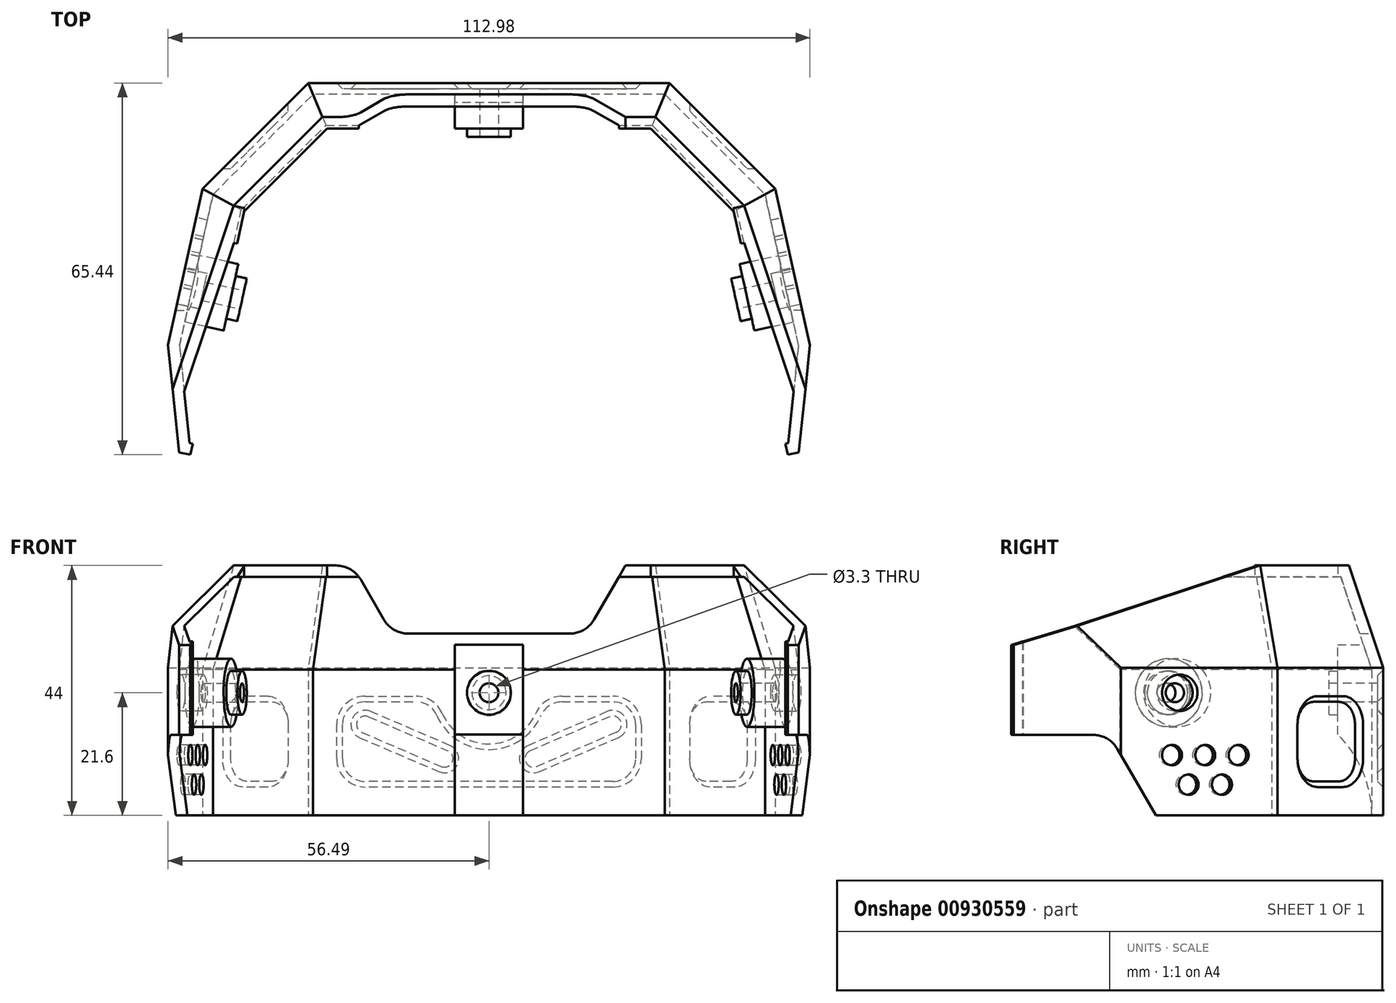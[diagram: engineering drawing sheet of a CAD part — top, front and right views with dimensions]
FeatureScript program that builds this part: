
annotation { "Feature Type Name" : "Feature", "Feature Type Description" : "" }
export const myFeature = defineFeature(function(context is Context, id is Id, definition is map)
    precondition{}
    {
        {
            var Q0;
            Q0=qCreatedBy(makeId("Top.planeOp"),FACE);
            var sketch = newSketch(context, id + "F0", { "sketchPlane" : qUnion([Q0])});
            skLineSegment(sketch, "E0", {"start": v(-18.54, 60) * mm, "end": v(18.54, 60) * mm, "construction": true});
            skArc(sketch, "E1", {"start": v(-18.54, 60) * mm, "mid": v(-31.06, 55.6) * mm, "end": v(-38.06, 44.32) * mm, "construction": true});
            skArc(sketch, "E2", {"start": v(38.06, 44.32) * mm, "mid": v(31.06, 55.6) * mm, "end": v(18.54, 60) * mm, "construction": true});
            skLineSegment(sketch, "E3", {"start": v(-38.06, 44.32) * mm, "end": v(-47.87, 0) * mm, "construction": true});
            skLineSegment(sketch, "E4", {"start": v(38.06, 44.32) * mm, "end": v(47.87, 0) * mm, "construction": true});
            skLineSegment(sketch, "E5", {"start": v(-44.1, 40.23) * mm, "end": v(-52.99, 0) * mm, "construction": true});
            skLineSegment(sketch, "E6", {"start": v(44.1, 40.23) * mm, "end": v(52.99, 0) * mm, "construction": true});
            skLineSegment(sketch, "E7", {"start": v(-44.1, 40.23) * mm, "end": v(-38.13, 44.03) * mm, "construction": true});
            skLineSegment(sketch, "E8", {"start": v(44.1, 40.23) * mm, "end": v(38.13, 44.03) * mm, "construction": true});
            skLineSegment(sketch, "E9", {"start": v(-52.99, 0) * mm, "end": v(52.99, 0) * mm, "construction": true});
            skLineSegment(sketch, "E10", {"start": v(-6, 60) * mm, "end": v(-6, 64) * mm, "construction": true});
            skLineSegment(sketch, "E11", {"start": v(-6, 64) * mm, "end": v(6, 64) * mm, "construction": true});
            skLineSegment(sketch, "E12", {"start": v(6, 64) * mm, "end": v(6, 60) * mm, "construction": true});
            skLineSegment(sketch, "E13", {"start": v(-45.4, 34.27) * mm, "end": v(-40.53, 33.19) * mm, "construction": true});
            skLineSegment(sketch, "E14", {"start": v(40.53, 33.19) * mm, "end": v(45.4, 34.27) * mm, "construction": true});
            skLineSegment(sketch, "E15", {"start": v(-28.48, 64) * mm, "end": v(28.48, 64) * mm});
            skLineSegment(sketch, "E16", {"start": v(-43.09, 49.39) * mm, "end": v(-52.56, 6.56) * mm});
            skLineSegment(sketch, "E17", {"start": v(43.09, 49.39) * mm, "end": v(52.56, 6.56) * mm});
            skLineSegment(sketch, "E18", {"start": v(-52.56, 6.56) * mm, "end": v(-60.37, 8.29) * mm});
            skLineSegment(sketch, "E19", {"start": v(-60.37, 8.29) * mm, "end": v(-50.4, 53.4) * mm});
            skLineSegment(sketch, "E20", {"start": v(52.56, 6.56) * mm, "end": v(60.37, 8.29) * mm});
            skLineSegment(sketch, "E21", {"start": v(60.37, 8.29) * mm, "end": v(50.4, 53.4) * mm});
            skLineSegment(sketch, "E22", {"start": v(-31.8, 72) * mm, "end": v(31.8, 72) * mm});
            skLineSegment(sketch, "E23", {"start": v(-28.48, 64) * mm, "end": v(-43.09, 49.39) * mm});
            skLineSegment(sketch, "E24", {"start": v(-50.4, 53.4) * mm, "end": v(-31.8, 72) * mm});
            skLineSegment(sketch, "E25", {"start": v(31.8, 72) * mm, "end": v(50.4, 53.4) * mm});
            skLineSegment(sketch, "E26", {"start": v(43.09, 49.39) * mm, "end": v(28.48, 64) * mm});
            skLineSegment(sketch, "E27", {"start": v(-45.4, 34.27) * mm, "end": v(-54.2, 36.21) * mm, "construction": true});
            skLineSegment(sketch, "E28", {"start": v(45.4, 34.27) * mm, "end": v(54.2, 36.21) * mm, "construction": true});
            skSolve(sketch);
        }
        {
            var Q0;
            Q0=qSketchRegion(id+"F0",true);
            extrude(context, id + "F1", {"entities" : qUnion([Q0]), "depth" : 44 * mm, "offsetDistance" : 25 * mm});
        }
        {
            var Q0;
            Q0=makeQuery(id+"F1.opExtrude","CAP_EDGE",EDGE,{"disambiguationData":[OSD([sQuery(id+"F0.wireOp",EDGE,"E19")])],"isStart":false});
            var Q1;
            Q1=makeQuery(id+"F1.opExtrude","CAP_EDGE",EDGE,{"disambiguationData":[OSD([sQuery(id+"F0.wireOp",EDGE,"E24")])],"isStart":false});
            var Q2;
            Q2=makeQuery(id+"F1.opExtrude","CAP_EDGE",EDGE,{"disambiguationData":[OSD([sQuery(id+"F0.wireOp",EDGE,"E22")])],"isStart":false});
            var Q3;
            Q3=makeQuery(id+"F1.opExtrude","CAP_EDGE",EDGE,{"disambiguationData":[OSD([sQuery(id+"F0.wireOp",EDGE,"E25")])],"isStart":false});
            var Q4;
            Q4=makeQuery(id+"F1.opExtrude","CAP_EDGE",EDGE,{"disambiguationData":[OSD([sQuery(id+"F0.wireOp",EDGE,"E21")])],"isStart":false});
            chamfer(context, id + "F2", {"entities" : qUnion([Q0, Q1, Q2, Q3, Q4]), "chamferType" : ChamferType.TWO_OFFSETS, "width1" : 18 * mm, "oppositeDirection" : false, "width2" : 6 * mm, "tangentPropagation" : true});
        }
        {
            var Q0;
            Q0=makeQuery(id+"F1.opExtrude","SWEPT_EDGE",EDGE,{"disambiguationData":[OSD([sQuery(id+"F0.wireOp",EDGE,"E18"),sQuery(id+"F0.wireOp",EDGE,"E19")])]});
            chamfer(context, id + "F3", {"entities" : qUnion([Q0]), "chamferType" : ChamferType.TWO_OFFSETS, "width1" : 6 * mm, "oppositeDirection" : false, "width2" : 18 * mm, "tangentPropagation" : true});
        }
        {
            var Q0;
            Q0=makeQuery(id+"F1.opExtrude","SWEPT_EDGE",EDGE,{"disambiguationData":[OSD([sQuery(id+"F0.wireOp",EDGE,"E20"),sQuery(id+"F0.wireOp",EDGE,"E21")])]});
            chamfer(context, id + "F4", {"entities" : qUnion([Q0]), "chamferType" : ChamferType.TWO_OFFSETS, "width1" : 18 * mm, "oppositeDirection" : false, "width2" : 6 * mm, "tangentPropagation" : true});
        }
        {
            var Q0;
            Q0=makeQuery(id+"F1.opExtrude","SWEPT_FACE",FACE,{"disambiguationData":[OSD([sQuery(id+"F0.wireOp",EDGE,"E15")])]});
            var Q1;
            Q1=makeQuery(id+"F1.opExtrude","SWEPT_FACE",FACE,{"disambiguationData":[OSD([sQuery(id+"F0.wireOp",EDGE,"E23")])]});
            var Q2;
            Q2=makeQuery(id+"F1.opExtrude","SWEPT_FACE",FACE,{"disambiguationData":[OSD([sQuery(id+"F0.wireOp",EDGE,"E16")])]});
            var Q3;
            Q3=makeQuery(id+"F1.opExtrude","SWEPT_FACE",FACE,{"disambiguationData":[OSD([sQuery(id+"F0.wireOp",EDGE,"E26")])]});
            var Q4;
            Q4=makeQuery(id+"F1.opExtrude","SWEPT_FACE",FACE,{"disambiguationData":[OSD([sQuery(id+"F0.wireOp",EDGE,"E17")])]});
            var Q5;
            Q5=makeQuery(id+"F1.opExtrude","CAP_FACE",FACE,{"disambiguationData":[OSD([sQuery(id+"F0.wireOp",EDGE,"E15"),sQuery(id+"F0.wireOp",EDGE,"E16"),sQuery(id+"F0.wireOp",EDGE,"E17"),sQuery(id+"F0.wireOp",EDGE,"E18"),sQuery(id+"F0.wireOp",EDGE,"E19"),sQuery(id+"F0.wireOp",EDGE,"E20"),sQuery(id+"F0.wireOp",EDGE,"E21"),sQuery(id+"F0.wireOp",EDGE,"E22"),sQuery(id+"F0.wireOp",EDGE,"E23"),sQuery(id+"F0.wireOp",EDGE,"E24"),sQuery(id+"F0.wireOp",EDGE,"E25"),sQuery(id+"F0.wireOp",EDGE,"E26")])],"isStart":true});
            shell(context, id + "F5", {"entities" : qUnion([Q0, Q1, Q2, Q3, Q4, Q5]), "thickness" : 2 * mm});
        }
        {
            var Q0;
            Q0=qCreatedBy(makeId("Right.planeOp"),FACE);
            var sketch = newSketch(context, id + "F6", { "sketchPlane" : qUnion([Q0])});
            skLineSegment(sketch, "E29", {"start": v(70, 25.68) * mm, "end": v(70, 0) * mm});
            skLineSegment(sketch, "E30", {"start": v(64, 14.24) * mm, "end": v(64, 30.04) * mm});
            skLineSegment(sketch, "E31", {"start": v(64, 30.04) * mm, "end": v(68.54, 30.04) * mm});
            skLineSegment(sketch, "E32", {"start": v(68.54, 30.04) * mm, "end": v(70, 25.68) * mm});
            skLineSegment(sketch, "E33.bottom", {"start": v(62, 30.04) * mm, "end": v(56, 30.04) * mm, "construction": true});
            skLineSegment(sketch, "E33.top", {"start": v(64, 14.24) * mm, "end": v(56, 14.24) * mm, "construction": true});
            skLineSegment(sketch, "E33.left", {"start": v(64, 28.04) * mm, "end": v(64, 14.24) * mm, "construction": true});
            skLineSegment(sketch, "E33.right", {"start": v(56, 30.04) * mm, "end": v(56, 14.24) * mm, "construction": true});
            skLineSegment(sketch, "E34", {"start": v(64, 28.04) * mm, "end": v(62, 30.04) * mm, "construction": true});
            skArc(sketch, "E35", {"start": v(70, 0) * mm, "mid": v(68.44, 7.73) * mm, "end": v(64, 14.24) * mm});
            skSolve(sketch);
        }
        {
            var Q0;
            Q0=qSketchRegion(id+"F6",true);
            extrude(context, id + "F7", {"entities" : qUnion([Q0]), "operationType" : NewBodyOperationType.ADD, "depth" : 6 * mm, "offsetDistance" : 25 * mm});
        }
        {
            var Q0;
            Q0=qSketchRegion(id+"F6",true);
            extrude(context, id + "F8", {"entities" : qUnion([Q0]), "operationType" : NewBodyOperationType.ADD, "oppositeDirection" : true, "depth" : 6 * mm, "offsetDistance" : 25 * mm});
        }
        {
            var Q0;
            {var subQ0=sQuery(id+"F6.wireOp",EDGE,"E30");Q0=makeQuery(id+"F8.boolean.opBoolean","MERGE",FACE,{"derivedFrom":[makeQuery(id+"F7.opExtrude","SWEPT_FACE",FACE,{"disambiguationData":[OSD([subQ0])]}),makeQuery(id+"F8.opExtrude","SWEPT_FACE",FACE,{"disambiguationData":[OSD([subQ0])]})]});}
            var sketch = newSketch(context, id + "F9", { "sketchPlane" : qUnion([Q0])});
            skCircle(sketch, "E36", {"center": v(0, 21.6) * mm, "radius": 3.85 * mm});
            skSolve(sketch);
        }
        {
            var Q0;
            Q0=qSketchRegion(id+"F9",true);
            extrude(context, id + "F10", {"entities" : qUnion([Q0]), "operationType" : NewBodyOperationType.ADD, "depth" : 1.5 * mm, "offsetDistance" : 25 * mm});
        }
        {
            var Q0;
            Q0=makeQuery(id+"F10.opExtrude","CAP_FACE",FACE,{"disambiguationData":[OSD([sQuery(id+"F9.wireOp",EDGE,"E36")])],"isStart":false});
            var sketch = newSketch(context, id + "F11", { "sketchPlane" : qUnion([Q0])});
            skCircle(sketch, "E37", {"center": v(0, 21.6) * mm, "radius": 1.65 * mm});
            skSolve(sketch);
        }
        {
            var Q0;
            Q0=qSketchRegion(id+"F11",true);
            extrude(context, id + "F12", {"entities" : qUnion([Q0]), "operationType" : NewBodyOperationType.REMOVE, "endBound" : BoundingType.UP_TO_NEXT, "oppositeDirection" : true, "depth" : 25 * mm, "offsetDistance" : 25 * mm});
        }
        {
            var Q0;
            Q0=makeQuery(id+"F1.opExtrude","SWEPT_FACE",FACE,{"disambiguationData":[OSD([sQuery(id+"F0.wireOp",EDGE,"E21")])]});
            var sketch = newSketch(context, id + "F13", { "sketchPlane" : qUnion([Q0])});
            skLineSegment(sketch, "E38", {"start": v(-4.95, 30) * mm, "end": v(39.5, 44) * mm});
            skLineSegment(sketch, "E39", {"start": v(39.5, 44) * mm, "end": v(-4.95, 44) * mm});
            skLineSegment(sketch, "E40", {"start": v(-4.95, 44) * mm, "end": v(-4.95, 30) * mm});
            skSolve(sketch);
        }
        {
            var Q0;
            Q0=qSketchRegion(id+"F13",true);
            var Q1;
            Q1=makeQuery(id+"F1.opExtrude","SWEPT_FACE",FACE,{"disambiguationData":[OSD([sQuery(id+"F0.wireOp",EDGE,"E17")])]});
            extrude(context, id + "F14", {"entities" : qUnion([Q0]), "operationType" : NewBodyOperationType.REMOVE, "endBound" : BoundingType.UP_TO_SURFACE, "oppositeDirection" : true, "depth" : 25 * mm, "endBoundEntityFace" : qUnion([Q1]), "offsetDistance" : 25 * mm});
        }
        {
            var Q0;
            Q0=makeQuery(id+"F1.opExtrude","SWEPT_FACE",FACE,{"disambiguationData":[OSD([sQuery(id+"F0.wireOp",EDGE,"E19")])]});
            var sketch = newSketch(context, id + "F15", { "sketchPlane" : qUnion([Q0])});
            skLineSegment(sketch, "E41", {"start": v(-39.5, 44) * mm, "end": v(4.95, 44) * mm});
            skLineSegment(sketch, "E42", {"start": v(4.95, 44) * mm, "end": v(4.95, 30) * mm});
            skLineSegment(sketch, "E43", {"start": v(4.95, 30) * mm, "end": v(-39.5, 44) * mm});
            skSolve(sketch);
        }
        {
            var Q0;
            Q0=qSketchRegion(id+"F15",true);
            var Q1;
            Q1=makeQuery(id+"F1.opExtrude","SWEPT_FACE",FACE,{"disambiguationData":[OSD([sQuery(id+"F0.wireOp",EDGE,"E16")])]});
            extrude(context, id + "F16", {"entities" : qUnion([Q0]), "operationType" : NewBodyOperationType.REMOVE, "endBound" : BoundingType.UP_TO_SURFACE, "oppositeDirection" : true, "depth" : 25 * mm, "endBoundEntityFace" : qUnion([Q1]), "offsetDistance" : 25 * mm});
        }
        {
            var Q0;
            Q0=qCreatedBy(makeId("Right.planeOp"),FACE);
            var sketch = newSketch(context, id + "F17", { "sketchPlane" : qUnion([Q0])});
            skLineSegment(sketch, "E44", {"start": v(32, 0) * mm, "end": v(23.8, 14.2) * mm});
            skLineSegment(sketch, "E45", {"start": v(23.8, 14.2) * mm, "end": v(6.56, 14.2) * mm});
            skLineSegment(sketch, "E46", {"start": v(6.56, 14.2) * mm, "end": v(6.56, 0) * mm});
            skLineSegment(sketch, "E47", {"start": v(6.56, 0) * mm, "end": v(32, 0) * mm});
            skCircle(sketch, "E48", {"center": v(14.7, 7) * mm, "radius": 10 * mm, "construction": true});
            skSolve(sketch);
        }
        {
            var Q0;
            Q0=qSketchRegion(id+"F17",true);
            var Q1;
            Q1=makeQuery(id+"F3.opChamfer","BLEND_FACE",FACE,{"disambiguationData":[OSD([sQuery(id+"F0.wireOp",EDGE,"E18"),sQuery(id+"F0.wireOp",EDGE,"E19")])]});
            extrude(context, id + "F18", {"entities" : qUnion([Q0]), "operationType" : NewBodyOperationType.REMOVE, "endBound" : BoundingType.UP_TO_SURFACE, "oppositeDirection" : true, "depth" : 25 * mm, "endBoundEntityFace" : qUnion([Q1]), "offsetDistance" : 25 * mm});
        }
        {
            var Q0;
            Q0=qSketchRegion(id+"F17",true);
            var Q1;
            Q1=makeQuery(id+"F4.opChamfer","BLEND_FACE",FACE,{"disambiguationData":[OSD([sQuery(id+"F0.wireOp",EDGE,"E20"),sQuery(id+"F0.wireOp",EDGE,"E21")])]});
            extrude(context, id + "F19", {"entities" : qUnion([Q0]), "operationType" : NewBodyOperationType.REMOVE, "endBound" : BoundingType.UP_TO_SURFACE, "depth" : 25 * mm, "endBoundEntityFace" : qUnion([Q1]), "offsetDistance" : 25 * mm});
        }
        {
            var Q0;
            Q0=makeQuery(id+"F1.opExtrude","SWEPT_FACE",FACE,{"disambiguationData":[OSD([sQuery(id+"F0.wireOp",EDGE,"E22")])]});
            var sketch = newSketch(context, id + "F20", { "sketchPlane" : qUnion([Q0])});
            skLineSegment(sketch, "E49", {"start": v(-24, 44) * mm, "end": v(24, 44) * mm});
            skLineSegment(sketch, "E50", {"start": v(24, 44) * mm, "end": v(17.07, 32) * mm});
            skLineSegment(sketch, "E51", {"start": v(17.07, 32) * mm, "end": v(-17.07, 32) * mm});
            skLineSegment(sketch, "E52", {"start": v(-17.07, 32) * mm, "end": v(-24, 44) * mm});
            skSolve(sketch);
        }
        {
            var Q0;
            Q0=qSketchRegion(id+"F20",true);
            var Q1;
            Q1=makeQuery(id+"F1.opExtrude","SWEPT_FACE",FACE,{"disambiguationData":[OSD([sQuery(id+"F0.wireOp",EDGE,"E15")])]});
            extrude(context, id + "F21", {"entities" : qUnion([Q0]), "operationType" : NewBodyOperationType.REMOVE, "endBound" : BoundingType.UP_TO_SURFACE, "oppositeDirection" : true, "depth" : 25 * mm, "endBoundEntityFace" : qUnion([Q1]), "offsetDistance" : 25 * mm});
        }
        {
            var Q0;
            Q0=makeQuery(id+"F21.boolean.opBoolean","COPY",EDGE,{"derivedFrom":makeQuery(id+"F21.opExtrude","SWEPT_EDGE",EDGE,{"disambiguationData":[OSD([sQuery(id+"F20.wireOp",EDGE,"E51"),sQuery(id+"F20.wireOp",EDGE,"E52")])]})});
            var Q1;
            Q1=makeQuery(id+"F21.boolean.opBoolean","COPY",EDGE,{"derivedFrom":makeQuery(id+"F21.opExtrude","SWEPT_EDGE",EDGE,{"disambiguationData":[OSD([sQuery(id+"F20.wireOp",EDGE,"E50"),sQuery(id+"F20.wireOp",EDGE,"E51")])]})});
            var Q2;
            Q2=makeQuery(id+"F21.boolean.opBoolean","COPY",EDGE,{"derivedFrom":makeQuery(id+"F21.opExtrude","SWEPT_EDGE",EDGE,{"disambiguationData":[OSD([sQuery(id+"F20.wireOp",EDGE,"E49"),sQuery(id+"F20.wireOp",EDGE,"E52")])]})});
            var Q3;
            Q3=makeQuery(id+"F21.boolean.opBoolean","COPY",EDGE,{"derivedFrom":makeQuery(id+"F21.opExtrude","SWEPT_EDGE",EDGE,{"disambiguationData":[OSD([sQuery(id+"F20.wireOp",EDGE,"E49"),sQuery(id+"F20.wireOp",EDGE,"E50")])]})});
            fillet(context, id + "F22", {"entities" : qUnion([Q0, Q1, Q2, Q3]), "radius" : 5 * mm, "tangentPropagation" : true, "allowEdgeOverflow" : false});
        }
        {
            var Q0;
            Q0=makeQuery(id+"F1.opExtrude","SWEPT_FACE",FACE,{"disambiguationData":[OSD([sQuery(id+"F0.wireOp",EDGE,"E22")])]});
            var sketch = newSketch(context, id + "F23", { "sketchPlane" : qUnion([Q0])});
            skLineSegment(sketch, "E53", {"start": v(-26.8, 16) * mm, "end": v(-26.8, 10) * mm});
            skLineSegment(sketch, "E54", {"start": v(-21.8, 5) * mm, "end": v(21.8, 5) * mm});
            skLineSegment(sketch, "E55", {"start": v(26.8, 10) * mm, "end": v(26.8, 16) * mm});
            skLineSegment(sketch, "E56", {"start": v(21.8, 21) * mm, "end": v(12.83, 21) * mm});
            skLineSegment(sketch, "E57", {"start": v(-12.83, 21) * mm, "end": v(-21.8, 21) * mm});
            skCircle(sketch, "E58", {"center": v(0, 21.6) * mm, "radius": 4 * mm});
            skArc(sketch, "E59", {"start": v(-8.25, 18) * mm, "mid": v(0, 12.6) * mm, "end": v(8.25, 18) * mm});
            skLineSegment(sketch, "E60", {"start": v(-21.2, 17.38) * mm, "end": v(-7.25, 11.38) * mm});
            skLineSegment(sketch, "E61", {"start": v(-22.38, 14.62) * mm, "end": v(-8.43, 8.62) * mm});
            skArc(sketch, "E62", {"start": v(-21.2, 17.38) * mm, "mid": v(-23.17, 16.6) * mm, "end": v(-22.38, 14.62) * mm});
            skArc(sketch, "E63", {"start": v(-8.43, 8.62) * mm, "mid": v(-6.46, 9.4) * mm, "end": v(-7.25, 11.38) * mm});
            skPoint(sketch, "E64.visualSharp", {"position": v(-26.8, 21) * mm});
            skArc(sketch, "E64.filletArc", {"start": v(-21.8, 21) * mm, "mid": v(-25.33, 19.54) * mm, "end": v(-26.8, 16) * mm});
            skPoint(sketch, "E65.visualSharp", {"position": v(-26.8, 5) * mm});
            skArc(sketch, "E65.filletArc", {"start": v(-26.8, 10) * mm, "mid": v(-25.33, 6.46) * mm, "end": v(-21.8, 5) * mm});
            skPoint(sketch, "E66.visualSharp", {"position": v(-8.98, 21) * mm});
            skArc(sketch, "E66.filletArc", {"start": v(-8.25, 18) * mm, "mid": v(-10.1, 20.18) * mm, "end": v(-12.83, 21) * mm});
            skPoint(sketch, "E67.visualSharp", {"position": v(8.98, 21) * mm});
            skArc(sketch, "E67.filletArc", {"start": v(12.83, 21) * mm, "mid": v(10.1, 20.18) * mm, "end": v(8.25, 18) * mm});
            skPoint(sketch, "E68.visualSharp", {"position": v(26.8, 21) * mm});
            skArc(sketch, "E68.filletArc", {"start": v(26.8, 16) * mm, "mid": v(25.33, 19.54) * mm, "end": v(21.8, 21) * mm});
            skPoint(sketch, "E69.visualSharp", {"position": v(26.8, 5) * mm});
            skArc(sketch, "E69.filletArc", {"start": v(21.8, 5) * mm, "mid": v(25.33, 6.46) * mm, "end": v(26.8, 10) * mm});
            skLineSegment(sketch, "E70", {"start": v(21.2, 17.38) * mm, "end": v(7.25, 11.38) * mm});
            skLineSegment(sketch, "E71", {"start": v(22.38, 14.62) * mm, "end": v(8.43, 8.62) * mm});
            skArc(sketch, "E72", {"start": v(22.38, 14.62) * mm, "mid": v(23.17, 16.6) * mm, "end": v(21.2, 17.38) * mm});
            skArc(sketch, "E73", {"start": v(7.25, 11.38) * mm, "mid": v(6.46, 9.4) * mm, "end": v(8.43, 8.62) * mm});
            skLineSegment(sketch, "E74", {"start": v(-7.84, 10) * mm, "end": v(-7.84, 5) * mm, "construction": true});
            skLineSegment(sketch, "E75", {"start": v(-7.84, 10) * mm, "end": v(-5.04, 14.14) * mm, "construction": true});
            skLineSegment(sketch, "E76", {"start": v(7.84, 10) * mm, "end": v(5.04, 14.14) * mm, "construction": true});
            skLineSegment(sketch, "E77", {"start": v(7.84, 10) * mm, "end": v(7.84, 5) * mm, "construction": true});
            skSolve(sketch);
        }
        {
            var Q0;
            Q0=qSketchRegion(id+"F23",true);
            extrude(context, id + "F24", {"entities" : qUnion([Q0]), "operationType" : NewBodyOperationType.REMOVE, "oppositeDirection" : true, "depth" : 1 * mm, "offsetDistance" : 25 * mm});
        }
        {
            var Q0;
            Q0=makeQuery(id+"F24.boolean.opBoolean","COPY",EDGE,{"derivedFrom":makeQuery(id+"F24.opExtrude","CAP_EDGE",EDGE,{"disambiguationData":[OSD([sQuery(id+"F23.wireOp",EDGE,"E59")])],"isStart":false})});
            var Q1;
            Q1=makeQuery(id+"F24.boolean.opBoolean","COPY",EDGE,{"derivedFrom":makeQuery(id+"F24.opExtrude","CAP_EDGE",EDGE,{"disambiguationData":[OSD([sQuery(id+"F23.wireOp",EDGE,"E61")])],"isStart":false})});
            var Q2;
            Q2=makeQuery(id+"F24.boolean.opBoolean","COPY",EDGE,{"derivedFrom":makeQuery(id+"F24.opExtrude","CAP_EDGE",EDGE,{"disambiguationData":[OSD([sQuery(id+"F23.wireOp",EDGE,"E71")])],"isStart":false})});
            var Q3;
            Q3=makeQuery(id+"F24.boolean.opBoolean","COPY",EDGE,{"derivedFrom":makeQuery(id+"F24.opExtrude","CAP_EDGE",EDGE,{"disambiguationData":[OSD([sQuery(id+"F23.wireOp",EDGE,"E58")])],"isStart":false})});
            chamfer(context, id + "F25", {"entities" : qUnion([Q0, Q1, Q2, Q3]), "width" : 1 * mm, "tangentPropagation" : true});
        }
        {
            var Q0;
            Q0=makeQuery(id+"F1.opExtrude","SWEPT_FACE",FACE,{"disambiguationData":[OSD([sQuery(id+"F0.wireOp",EDGE,"E25")])]});
            var sketch = newSketch(context, id + "F26", { "sketchPlane" : qUnion([Q0])});
            skLineSegment(sketch, "E78.bottom", {"start": v(12.12, 21) * mm, "end": v(18.43, 21) * mm});
            skLineSegment(sketch, "E78.top", {"start": v(12.12, 5) * mm, "end": v(18.43, 5) * mm});
            skLineSegment(sketch, "E78.left", {"start": v(7.12, 16) * mm, "end": v(7.12, 10) * mm});
            skLineSegment(sketch, "E78.right", {"start": v(23.43, 16) * mm, "end": v(23.43, 10) * mm});
            skPoint(sketch, "E79.visualSharp", {"position": v(7.12, 21) * mm});
            skArc(sketch, "E79.filletArc", {"start": v(12.12, 21) * mm, "mid": v(8.59, 19.54) * mm, "end": v(7.12, 16) * mm});
            skPoint(sketch, "E80.visualSharp", {"position": v(7.12, 5) * mm});
            skArc(sketch, "E80.filletArc", {"start": v(7.12, 10) * mm, "mid": v(8.59, 6.46) * mm, "end": v(12.12, 5) * mm});
            skPoint(sketch, "E81.visualSharp", {"position": v(23.43, 5) * mm});
            skArc(sketch, "E81.filletArc", {"start": v(18.43, 5) * mm, "mid": v(21.97, 6.46) * mm, "end": v(23.43, 10) * mm});
            skPoint(sketch, "E82.visualSharp", {"position": v(23.43, 21) * mm});
            skArc(sketch, "E82.filletArc", {"start": v(23.43, 16) * mm, "mid": v(21.97, 19.54) * mm, "end": v(18.43, 21) * mm});
            skSolve(sketch);
        }
        {
            var Q0;
            Q0=qSketchRegion(id+"F26",true);
            extrude(context, id + "F27", {"entities" : qUnion([Q0]), "operationType" : NewBodyOperationType.REMOVE, "oppositeDirection" : true, "depth" : 1 * mm, "offsetDistance" : 25 * mm});
        }
        {
            var Q0;
            Q0=makeQuery(id+"F27.boolean.opBoolean","COPY",EDGE,{"derivedFrom":makeQuery(id+"F27.opExtrude","CAP_EDGE",EDGE,{"disambiguationData":[OSD([sQuery(id+"F26.wireOp",EDGE,"E79.filletArc")])],"isStart":false})});
            chamfer(context, id + "F28", {"entities" : qUnion([Q0]), "width" : 1 * mm, "tangentPropagation" : true});
        }
        {
            var Q0;
            Q0=makeQuery(id+"F1.opExtrude","SWEPT_FACE",FACE,{"disambiguationData":[OSD([sQuery(id+"F0.wireOp",EDGE,"E24")])]});
            var sketch = newSketch(context, id + "F29", { "sketchPlane" : qUnion([Q0])});
            skLineSegment(sketch, "E83.bottom", {"start": v(-18.43, 21) * mm, "end": v(-12.12, 21) * mm});
            skLineSegment(sketch, "E83.top", {"start": v(-18.43, 5) * mm, "end": v(-12.12, 5) * mm});
            skLineSegment(sketch, "E83.left", {"start": v(-23.43, 16) * mm, "end": v(-23.43, 10) * mm});
            skLineSegment(sketch, "E83.right", {"start": v(-7.12, 16) * mm, "end": v(-7.12, 10) * mm});
            skPoint(sketch, "E84.visualSharp", {"position": v(-23.43, 21) * mm});
            skArc(sketch, "E84.filletArc", {"start": v(-18.43, 21) * mm, "mid": v(-21.97, 19.54) * mm, "end": v(-23.43, 16) * mm});
            skPoint(sketch, "E85.visualSharp", {"position": v(-23.43, 5) * mm});
            skArc(sketch, "E85.filletArc", {"start": v(-23.43, 10) * mm, "mid": v(-21.97, 6.46) * mm, "end": v(-18.43, 5) * mm});
            skPoint(sketch, "E86.visualSharp", {"position": v(-7.12, 5) * mm});
            skArc(sketch, "E86.filletArc", {"start": v(-12.12, 5) * mm, "mid": v(-8.59, 6.46) * mm, "end": v(-7.12, 10) * mm});
            skPoint(sketch, "E87.visualSharp", {"position": v(-7.12, 21) * mm});
            skArc(sketch, "E87.filletArc", {"start": v(-7.12, 16) * mm, "mid": v(-8.59, 19.54) * mm, "end": v(-12.12, 21) * mm});
            skSolve(sketch);
        }
        {
            var Q0;
            Q0=qSketchRegion(id+"F29",true);
            extrude(context, id + "F30", {"entities" : qUnion([Q0]), "operationType" : NewBodyOperationType.REMOVE, "oppositeDirection" : true, "depth" : 1 * mm, "offsetDistance" : 25 * mm});
        }
        {
            var Q0;
            Q0=makeQuery(id+"F30.boolean.opBoolean","COPY",EDGE,{"derivedFrom":makeQuery(id+"F30.opExtrude","CAP_EDGE",EDGE,{"disambiguationData":[OSD([sQuery(id+"F29.wireOp",EDGE,"E84.filletArc")])],"isStart":false})});
            chamfer(context, id + "F31", {"entities" : qUnion([Q0]), "width" : 1 * mm, "tangentPropagation" : true});
        }
        {
            var Q0;
            {var subQ0=sQuery(id+"F0.wireOp",EDGE,"E19");Q0=makeQuery(id+"F5.opShell","OFFSET_FACE",FACE,{"disambiguationData":[OSD([subQ0]),TDD([makeQuery(id+"F1.opExtrude","SWEPT_FACE",FACE,{"disambiguationData":[OSD([subQ0])]})])]});}
            var sketch = newSketch(context, id + "F32", { "sketchPlane" : qUnion([Q0])});
            skCircle(sketch, "E88", {"center": v(23.65, 21.6) * mm, "radius": 6 * mm});
            skSolve(sketch);
        }
        {
            var Q0;
            Q0=qSketchRegion(id+"F32",true);
            extrude(context, id + "F33", {"entities" : qUnion([Q0]), "operationType" : NewBodyOperationType.ADD, "depth" : 7 * mm, "offsetDistance" : 25 * mm});
        }
        {
            var Q0;
            {var subQ0=sQuery(id+"F0.wireOp",EDGE,"E21");Q0=makeQuery(id+"F5.opShell","OFFSET_FACE",FACE,{"disambiguationData":[OSD([subQ0]),TDD([makeQuery(id+"F1.opExtrude","SWEPT_FACE",FACE,{"disambiguationData":[OSD([subQ0])]})])]});}
            var sketch = newSketch(context, id + "F34", { "sketchPlane" : qUnion([Q0])});
            skCircle(sketch, "E89", {"center": v(-23.65, 21.6) * mm, "radius": 6 * mm});
            skSolve(sketch);
        }
        {
            var Q0;
            Q0=qSketchRegion(id+"F34",true);
            extrude(context, id + "F35", {"entities" : qUnion([Q0]), "operationType" : NewBodyOperationType.ADD, "depth" : 7 * mm, "offsetDistance" : 25 * mm});
        }
        {
            var Q0;
            Q0=makeQuery(id+"F35.opExtrude","CAP_FACE",FACE,{"disambiguationData":[OSD([sQuery(id+"F34.wireOp",EDGE,"E89")])],"isStart":false});
            var sketch = newSketch(context, id + "F36", { "sketchPlane" : qUnion([Q0])});
            skCircle(sketch, "E90", {"center": v(-23.65, 21.6) * mm, "radius": 3.85 * mm});
            skSolve(sketch);
        }
        {
            var Q0;
            Q0=qSketchRegion(id+"F36",true);
            extrude(context, id + "F37", {"entities" : qUnion([Q0]), "operationType" : NewBodyOperationType.ADD, "depth" : 2 * mm, "offsetDistance" : 25 * mm});
        }
        {
            var Q0;
            Q0=makeQuery(id+"F33.opExtrude","CAP_FACE",FACE,{"disambiguationData":[OSD([sQuery(id+"F32.wireOp",EDGE,"E88")])],"isStart":false});
            var sketch = newSketch(context, id + "F38", { "sketchPlane" : qUnion([Q0])});
            skCircle(sketch, "E91", {"center": v(23.65, 21.6) * mm, "radius": 3.85 * mm});
            skSolve(sketch);
        }
        {
            var Q0;
            Q0=qSketchRegion(id+"F38",true);
            extrude(context, id + "F39", {"entities" : qUnion([Q0]), "operationType" : NewBodyOperationType.ADD, "depth" : 2 * mm, "offsetDistance" : 25 * mm});
        }
        {
            var Q0;
            Q0=makeQuery(id+"F37.opExtrude","CAP_FACE",FACE,{"disambiguationData":[OSD([sQuery(id+"F36.wireOp",EDGE,"E90")])],"isStart":false});
            var sketch = newSketch(context, id + "F40", { "sketchPlane" : qUnion([Q0])});
            skCircle(sketch, "E92", {"center": v(-23.65, 21.6) * mm, "radius": 1.65 * mm});
            skSolve(sketch);
        }
        {
            var Q0;
            Q0=qSketchRegion(id+"F40",true);
            extrude(context, id + "F41", {"entities" : qUnion([Q0]), "operationType" : NewBodyOperationType.REMOVE, "endBound" : BoundingType.UP_TO_NEXT, "oppositeDirection" : true, "depth" : 25 * mm, "offsetDistance" : 25 * mm});
        }
        {
            var Q0;
            Q0=makeQuery(id+"F39.opExtrude","CAP_FACE",FACE,{"disambiguationData":[OSD([sQuery(id+"F38.wireOp",EDGE,"E91")])],"isStart":false});
            var sketch = newSketch(context, id + "F42", { "sketchPlane" : qUnion([Q0])});
            skCircle(sketch, "E93", {"center": v(23.65, 21.6) * mm, "radius": 1.65 * mm});
            skSolve(sketch);
        }
        {
            var Q0;
            Q0=qSketchRegion(id+"F42",true);
            extrude(context, id + "F43", {"entities" : qUnion([Q0]), "operationType" : NewBodyOperationType.REMOVE, "endBound" : BoundingType.UP_TO_NEXT, "oppositeDirection" : true, "depth" : 25 * mm, "offsetDistance" : 25 * mm});
        }
        {
            var Q0;
            Q0=makeQuery(id+"F1.opExtrude","SWEPT_FACE",FACE,{"disambiguationData":[OSD([sQuery(id+"F0.wireOp",EDGE,"E19")])]});
            var sketch = newSketch(context, id + "F44", { "sketchPlane" : qUnion([Q0])});
            skCircle(sketch, "E94", {"center": v(-23.65, 21.6) * mm, "radius": 3.2 * mm});
            skSolve(sketch);
        }
        {
            var Q0;
            Q0=qSketchRegion(id+"F44",true);
            extrude(context, id + "F45", {"entities" : qUnion([Q0]), "operationType" : NewBodyOperationType.REMOVE, "oppositeDirection" : true, "depth" : 4 * mm, "offsetDistance" : 25 * mm});
        }
        {
            var Q0;
            Q0=makeQuery(id+"F1.opExtrude","SWEPT_FACE",FACE,{"disambiguationData":[OSD([sQuery(id+"F0.wireOp",EDGE,"E21")])]});
            var sketch = newSketch(context, id + "F46", { "sketchPlane" : qUnion([Q0])});
            skCircle(sketch, "E95", {"center": v(23.65, 21.6) * mm, "radius": 3.2 * mm});
            skSolve(sketch);
        }
        {
            var Q0;
            Q0=qSketchRegion(id+"F46",true);
            extrude(context, id + "F47", {"entities" : qUnion([Q0]), "operationType" : NewBodyOperationType.REMOVE, "oppositeDirection" : true, "depth" : 4 * mm, "offsetDistance" : 25 * mm});
        }
        {
            var Q0;
            Q0=makeQuery(id+"F1.opExtrude","SWEPT_FACE",FACE,{"disambiguationData":[OSD([sQuery(id+"F0.wireOp",EDGE,"E21")])]});
            var sketch = newSketch(context, id + "F48", { "sketchPlane" : qUnion([Q0])});
            skLineSegment(sketch, "E96", {"start": v(22.25, 10.63) * mm, "end": v(25.25, 5.43) * mm, "construction": true});
            skLineSegment(sketch, "E97", {"start": v(25.25, 5.43) * mm, "end": v(28.25, 10.63) * mm, "construction": true});
            skLineSegment(sketch, "E98", {"start": v(28.25, 10.63) * mm, "end": v(22.25, 10.63) * mm, "construction": true});
            skLineSegment(sketch, "E99", {"start": v(28.25, 10.63) * mm, "end": v(34.25, 10.63) * mm, "construction": true});
            skLineSegment(sketch, "E100", {"start": v(34.25, 10.63) * mm, "end": v(31.25, 5.43) * mm, "construction": true});
            skLineSegment(sketch, "E101", {"start": v(31.25, 5.43) * mm, "end": v(28.25, 10.63) * mm, "construction": true});
            skLineSegment(sketch, "E102", {"start": v(25.25, 5.43) * mm, "end": v(31.25, 5.43) * mm, "construction": true});
            skCircle(sketch, "E103", {"center": v(22.25, 10.63) * mm, "radius": 1.8 * mm});
            skCircle(sketch, "E104", {"center": v(28.25, 10.63) * mm, "radius": 1.8 * mm});
            skCircle(sketch, "E105", {"center": v(34.25, 10.63) * mm, "radius": 1.8 * mm});
            skCircle(sketch, "E106", {"center": v(25.25, 5.43) * mm, "radius": 1.8 * mm});
            skCircle(sketch, "E107", {"center": v(31.25, 5.43) * mm, "radius": 1.8 * mm});
            skLineSegment(sketch, "E108", {"start": v(22.25, 10.63) * mm, "end": v(13.05, 10.63) * mm, "construction": true});
            skLineSegment(sketch, "E109", {"start": v(34.25, 10.63) * mm, "end": v(41.25, 10.63) * mm, "construction": true});
            skSolve(sketch);
        }
        {
            var Q0;
            Q0=qSketchRegion(id+"F48",true);
            extrude(context, id + "F49", {"entities" : qUnion([Q0]), "operationType" : NewBodyOperationType.REMOVE, "endBound" : BoundingType.UP_TO_NEXT, "oppositeDirection" : true, "depth" : 25 * mm, "offsetDistance" : 25 * mm});
        }
        {
            var Q0;
            Q0=makeQuery(id+"F1.opExtrude","SWEPT_FACE",FACE,{"disambiguationData":[OSD([sQuery(id+"F0.wireOp",EDGE,"E19")])]});
            var sketch = newSketch(context, id + "F50", { "sketchPlane" : qUnion([Q0])});
            skLineSegment(sketch, "E110", {"start": v(-34.25, 10.63) * mm, "end": v(-28.25, 10.63) * mm, "construction": true});
            skLineSegment(sketch, "E111", {"start": v(-28.25, 10.63) * mm, "end": v(-22.25, 10.63) * mm, "construction": true});
            skLineSegment(sketch, "E112", {"start": v(-22.25, 10.63) * mm, "end": v(-25.25, 5.43) * mm, "construction": true});
            skLineSegment(sketch, "E113", {"start": v(-25.25, 5.43) * mm, "end": v(-28.25, 10.63) * mm, "construction": true});
            skLineSegment(sketch, "E114", {"start": v(-34.25, 10.63) * mm, "end": v(-31.25, 5.43) * mm, "construction": true});
            skLineSegment(sketch, "E115", {"start": v(-31.25, 5.43) * mm, "end": v(-28.25, 10.63) * mm, "construction": true});
            skLineSegment(sketch, "E116", {"start": v(-31.25, 5.43) * mm, "end": v(-25.25, 5.43) * mm, "construction": true});
            skLineSegment(sketch, "E117", {"start": v(-22.25, 10.63) * mm, "end": v(-13.05, 10.63) * mm, "construction": true});
            skCircle(sketch, "E118", {"center": v(-34.25, 10.63) * mm, "radius": 1.8 * mm});
            skCircle(sketch, "E119", {"center": v(-31.25, 5.43) * mm, "radius": 1.8 * mm});
            skCircle(sketch, "E120", {"center": v(-28.25, 10.63) * mm, "radius": 1.8 * mm});
            skCircle(sketch, "E121", {"center": v(-25.25, 5.43) * mm, "radius": 1.8 * mm});
            skCircle(sketch, "E122", {"center": v(-22.25, 10.63) * mm, "radius": 1.8 * mm});
            skLineSegment(sketch, "E123", {"start": v(-34.25, 10.63) * mm, "end": v(-41.25, 10.63) * mm, "construction": true});
            skSolve(sketch);
        }
        {
            var Q0;
            Q0=qSketchRegion(id+"F50",true);
            extrude(context, id + "F51", {"entities" : qUnion([Q0]), "operationType" : NewBodyOperationType.REMOVE, "endBound" : BoundingType.UP_TO_NEXT, "oppositeDirection" : true, "depth" : 25 * mm, "offsetDistance" : 25 * mm});
        }
        {
            var Q0;
            Q0=makeQuery(id+"F19.boolean.opBoolean","COPY",EDGE,{"derivedFrom":makeQuery(id+"F19.opExtrude","SWEPT_EDGE",EDGE,{"disambiguationData":[OSD([sQuery(id+"F17.wireOp",EDGE,"E44"),sQuery(id+"F17.wireOp",EDGE,"E45")])]})});
            var Q1;
            Q1=makeQuery(id+"F18.boolean.opBoolean","COPY",EDGE,{"derivedFrom":makeQuery(id+"F18.opExtrude","SWEPT_EDGE",EDGE,{"disambiguationData":[OSD([sQuery(id+"F17.wireOp",EDGE,"E44"),sQuery(id+"F17.wireOp",EDGE,"E45")])]})});
            fillet(context, id + "F52", {"entities" : qUnion([Q0, Q1]), "radius" : 5 * mm, "tangentPropagation" : true, "allowEdgeOverflow" : false});
        }
    });
